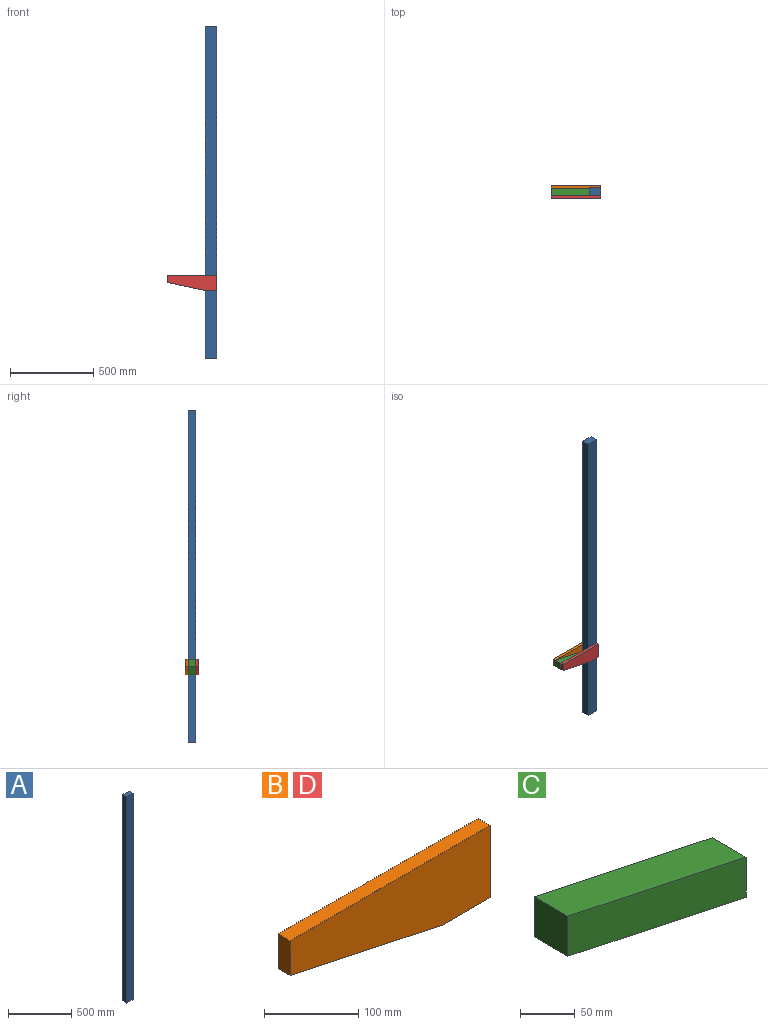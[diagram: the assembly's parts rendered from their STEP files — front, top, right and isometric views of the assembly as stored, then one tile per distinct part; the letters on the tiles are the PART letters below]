
ASSEMBLY  parts=4 mates=3
PART A: 6 faces, bbox 69x44x2000 mm
  f0: plane 2000x69mm, normal (0,1,0), area 138000mm2, adj f1,f3,f4,f5
  f1: plane 2000x44mm, normal (-1,0,0), area 88000mm2, adj f0,f2,f4,f5
  f2: plane 2000x69mm, normal (0,-1,0), area 138000mm2, adj f1,f3,f4,f5
  f3: plane 2000x44mm, normal (1,0,0), area 88000mm2, adj f0,f2,f4,f5
  f4: plane 69x44mm, normal (0,0,1), area 3036mm2, adj f0,f1,f2,f3
  f5: plane 69x44mm, normal (0,0,-1), area 3036mm2, adj f0,f1,f2,f3
PART B: 7 faces, bbox 300x18x94 mm
  f0: plane 300x18mm, normal (0,0,1), area 5400mm2, adj f1,f4,f5,f6
  f1: plane 45x18mm, normal (-1,0,0), area 810mm2, adj f0,f2,f5,f6
  f2: plane 230x49mm, normal (-0.21,0,-0.98), area 4232.9mm2, adj f1,f3,f5,f6
  f3: plane 70x18mm, normal (0,0,-1), area 1260mm2, adj f2,f4,f5,f6
  f4: plane 94x18mm, normal (1,0,0), area 1692mm2, adj f0,f3,f5,f6
  f5: plane 300x94mm, normal (0,-1,0), area 22565mm2, adj f0,f1,f2,f3,f4
  f6: plane 300x94mm, normal (0,1,0), area 22565mm2, adj f0,f1,f2,f3,f4
PART C: 7 faces, bbox 231x44x94 mm
  f0: plane 44.77x44mm, normal (1,0,0), area 1970.1mm2, adj f1,f4,f5,f6
  f1: plane 231x49.21mm, normal (0.21,0,0.98), area 10392.1mm2, adj f0,f2,f5,f6
  f2: plane 44.99x44mm, normal (-1,0,0), area 1979.4mm2, adj f1,f3,f5,f6
  f3: plane 230x49mm, normal (-0.21,0,-0.98), area 10347.1mm2, adj f2,f4,f5,f6
  f4: plane 44x1mm, normal (0,0,-1), area 44mm2, adj f0,f3,f5,f6
  f5: plane 231x93.99mm, normal (0,-1,0), area 10392mm2, adj f0,f1,f2,f3,f4
  f6: plane 231x93.99mm, normal (0,1,0), area 10392mm2, adj f0,f1,f2,f3,f4
PART D: same geometry as B
PLACE A t=(151.35,-117.85,-1.53)mm fixed
PLACE B t=(225.96,18.47,241.53)mm
PLACE C t=(225.96,18.47,241.53)mm
PLACE D t=(225.96,-43.53,241.53)mm
MATE planar B.f5 <-> A.f0  axis (0,-1,0) through (-1.14,0.47,498.47)mm
MATE planar B.f5 <-> C.f6  axis (0,-1,0) through (-301.14,0.47,453.47)mm
MATE planar C.f5 <-> D.f6  axis (0,-1,0) through (-301.14,-43.53,453.47)mm
